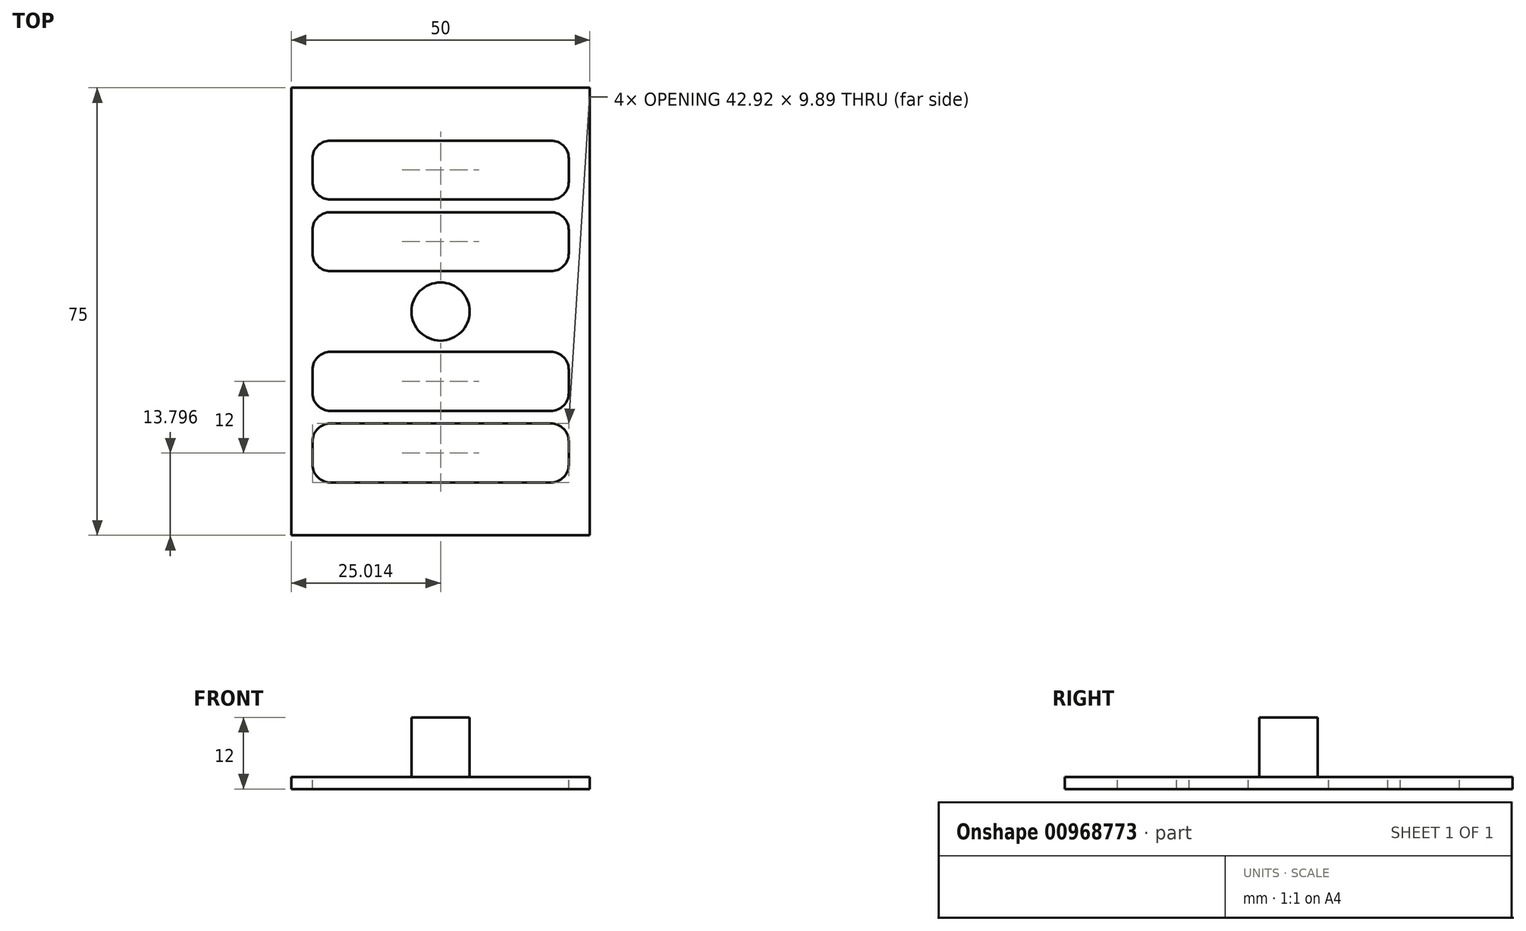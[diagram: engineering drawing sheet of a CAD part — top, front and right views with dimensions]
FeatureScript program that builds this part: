
annotation { "Feature Type Name" : "Feature", "Feature Type Description" : "" }
export const myFeature = defineFeature(function(context is Context, id is Id, definition is map)
    precondition{}
    {
        {
            var Q0;
            Q0=qCreatedBy(makeId("Top.planeOp"),FACE);
            var sketch = newSketch(context, id + "F0", { "sketchPlane" : qUnion([Q0])});
            skLineSegment(sketch, "E0.bottom", {"start": v(25, -37.5) * mm, "end": v(-25, -37.5) * mm});
            skLineSegment(sketch, "E0.top", {"start": v(25, 37.5) * mm, "end": v(-25, 37.5) * mm});
            skLineSegment(sketch, "E0.left", {"start": v(25, -37.5) * mm, "end": v(25, 37.5) * mm});
            skLineSegment(sketch, "E0.right", {"start": v(-25, -37.5) * mm, "end": v(-25, 37.5) * mm});
            skPoint(sketch, "E0.middle", {"position": v(0, 0) * mm});
            skSolve(sketch);
        }
        {
            var Q0;
            Q0=makeQuery(id+"F0.imprint","IMPRINT",FACE,{"disambiguationData":[TD([[makeQuery(id+"F0.imprint","IMPRINT",EDGE,{"derivedFrom":sQuery(id+"F0.wireOp",EDGE,"E0.bottom")}),-1.0]])]});
            extrude(context, id + "F1", {"entities" : qUnion([Q0]), "depth" : 2 * mm, "offsetDistance" : 25 * mm});
        }
        {
            var Q0;
            Q0=makeQuery(id+"FOSmCHiaZBp4P99_1.boolean.opBoolean","MERGE",FACE,{"derivedFrom":[makeQuery(id+"F1.opExtrude","CAP_FACE",FACE,{"disambiguationData":[OSD([sQuery(id+"F0.wireOp",EDGE,"E0.bottom"),sQuery(id+"F0.wireOp",EDGE,"E0.top"),sQuery(id+"F0.wireOp",EDGE,"E0.left"),sQuery(id+"F0.wireOp",EDGE,"E0.right")])],"isStart":false}),makeQuery(id+"FOSmCHiaZBp4P99_1.opExtrude","CAP_FACE",FACE,{"disambiguationData":[OSD([sQuery(id+"F7uODuXZmuw1LMT_1.wireOp",EDGE,"ikZA7m4t-yXm2-VDTh-IuRp-0IEzlSagpjaw.bottom"),sQuery(id+"F7uODuXZmuw1LMT_1.wireOp",EDGE,"ikZA7m4t-yXm2-VDTh-IuRp-0IEzlSagpjaw.left"),sQuery(id+"F7uODuXZmuw1LMT_1.wireOp",EDGE,"ikZA7m4t-yXm2-VDTh-IuRp-0IEzlSagpjaw.right"),sQuery(id+"F7uODuXZmuw1LMT_1.wireOp",EDGE,"wiYl6r0H-u17V-zEIH-iWu8-kZRWzZkrRSte"),sQuery(id+"F7uODuXZmuw1LMT_1.wireOp",EDGE,"84bd39a7-035e-4810-80ba-21c04ed16744.filletArc"),sQuery(id+"F7uODuXZmuw1LMT_1.wireOp",EDGE,"90e38472-87f6-4bb7-9f87-e36e951d7eac.filletArc")])],"isStart":false}),makeQuery(id+"FOSmCHiaZBp4P99_1.opExtrude","CAP_FACE",FACE,{"disambiguationData":[OSD([sQuery(id+"F7uODuXZmuw1LMT_1.wireOp",EDGE,"83aa809a-4b3d-4665-bd88-ce5ddef207420.MirrorCS"),sQuery(id+"F7uODuXZmuw1LMT_1.wireOp",EDGE,"7f4b2661-4254-4edf-b199-c165164cc8980.MirrorCS"),sQuery(id+"F7uODuXZmuw1LMT_1.wireOp",EDGE,"fd2b38a9-e8a0-4511-baa7-e9677021980d0.MirrorCS"),sQuery(id+"F7uODuXZmuw1LMT_1.wireOp",EDGE,"173fde81-6119-4368-834b-0b8efb7ed5110.MirrorCS"),sQuery(id+"F7uODuXZmuw1LMT_1.wireOp",EDGE,"5b3da9ca-773f-4fe3-a15f-effaa47ec4bf0.MirrorCS"),sQuery(id+"F7uODuXZmuw1LMT_1.wireOp",EDGE,"6c969054-023f-4f27-a523-787d0daa6e270.MirrorCS")])],"isStart":false})]});
            var sketch = newSketch(context, id + "F2", { "sketchPlane" : qUnion([Q0])});
            skCircle(sketch, "E1", {"center": v(0, 0) * mm, "radius": 4.88 * mm});
            skSolve(sketch);
        }
        {
            var Q0;
            Q0=makeQuery(id+"F2.imprint","IMPRINT",FACE,{"disambiguationData":[TD([[makeQuery(id+"F2.imprint","IMPRINT",EDGE,{"derivedFrom":sQuery(id+"F2.wireOp",EDGE,"E1")}),1.0]])]});
            extrude(context, id + "F3", {"entities" : qUnion([Q0]), "operationType" : NewBodyOperationType.ADD, "depth" : 10 * mm, "offsetDistance" : 25 * mm});
        }
        {
            var Q0;
            Q0=makeQuery(id+"FOSmCHiaZBp4P99_1.boolean.opBoolean","MERGE",FACE,{"derivedFrom":[makeQuery(id+"F1.opExtrude","CAP_FACE",FACE,{"disambiguationData":[OSD([sQuery(id+"F0.wireOp",EDGE,"E0.bottom"),sQuery(id+"F0.wireOp",EDGE,"E0.top"),sQuery(id+"F0.wireOp",EDGE,"E0.left"),sQuery(id+"F0.wireOp",EDGE,"E0.right")])],"isStart":false}),makeQuery(id+"FOSmCHiaZBp4P99_1.opExtrude","CAP_FACE",FACE,{"disambiguationData":[OSD([sQuery(id+"F7uODuXZmuw1LMT_1.wireOp",EDGE,"ikZA7m4t-yXm2-VDTh-IuRp-0IEzlSagpjaw.bottom"),sQuery(id+"F7uODuXZmuw1LMT_1.wireOp",EDGE,"ikZA7m4t-yXm2-VDTh-IuRp-0IEzlSagpjaw.left"),sQuery(id+"F7uODuXZmuw1LMT_1.wireOp",EDGE,"ikZA7m4t-yXm2-VDTh-IuRp-0IEzlSagpjaw.right"),sQuery(id+"F7uODuXZmuw1LMT_1.wireOp",EDGE,"wiYl6r0H-u17V-zEIH-iWu8-kZRWzZkrRSte"),sQuery(id+"F7uODuXZmuw1LMT_1.wireOp",EDGE,"84bd39a7-035e-4810-80ba-21c04ed16744.filletArc"),sQuery(id+"F7uODuXZmuw1LMT_1.wireOp",EDGE,"90e38472-87f6-4bb7-9f87-e36e951d7eac.filletArc")])],"isStart":false}),makeQuery(id+"FOSmCHiaZBp4P99_1.opExtrude","CAP_FACE",FACE,{"disambiguationData":[OSD([sQuery(id+"F7uODuXZmuw1LMT_1.wireOp",EDGE,"83aa809a-4b3d-4665-bd88-ce5ddef207420.MirrorCS"),sQuery(id+"F7uODuXZmuw1LMT_1.wireOp",EDGE,"7f4b2661-4254-4edf-b199-c165164cc8980.MirrorCS"),sQuery(id+"F7uODuXZmuw1LMT_1.wireOp",EDGE,"fd2b38a9-e8a0-4511-baa7-e9677021980d0.MirrorCS"),sQuery(id+"F7uODuXZmuw1LMT_1.wireOp",EDGE,"173fde81-6119-4368-834b-0b8efb7ed5110.MirrorCS"),sQuery(id+"F7uODuXZmuw1LMT_1.wireOp",EDGE,"5b3da9ca-773f-4fe3-a15f-effaa47ec4bf0.MirrorCS"),sQuery(id+"F7uODuXZmuw1LMT_1.wireOp",EDGE,"6c969054-023f-4f27-a523-787d0daa6e270.MirrorCS")])],"isStart":false})]});
            var sketch = newSketch(context, id + "F4", { "sketchPlane" : qUnion([Q0])});
            skLineSegment(sketch, "E2.bottom", {"start": v(-18.44, 16.65) * mm, "end": v(18.47, 16.65) * mm});
            skLineSegment(sketch, "E2.top", {"start": v(-18.44, 6.76) * mm, "end": v(18.47, 6.76) * mm});
            skLineSegment(sketch, "E2.left", {"start": v(-21.44, 13.65) * mm, "end": v(-21.44, 9.76) * mm});
            skLineSegment(sketch, "E2.right", {"start": v(21.47, 13.65) * mm, "end": v(21.47, 9.76) * mm});
            skLineSegment(sketch, "E3.MirrorCS", {"start": v(21.47, -13.65) * mm, "end": v(21.47, -9.76) * mm});
            skLineSegment(sketch, "E4.MirrorCS", {"start": v(-21.44, -13.65) * mm, "end": v(-21.44, -9.76) * mm});
            skLineSegment(sketch, "E5.MirrorCS", {"start": v(-18.44, -16.65) * mm, "end": v(18.47, -16.65) * mm});
            skLineSegment(sketch, "E6.MirrorCS", {"start": v(-18.44, -6.76) * mm, "end": v(18.47, -6.76) * mm});
            skPoint(sketch, "E7.visualSharp", {"position": v(-21.44, 16.65) * mm});
            skArc(sketch, "E7.filletArc", {"start": v(-18.44, 16.65) * mm, "mid": v(-20.57, 15.77) * mm, "end": v(-21.44, 13.65) * mm});
            skPoint(sketch, "E8.visualSharp", {"position": v(-21.44, 6.76) * mm});
            skArc(sketch, "E8.filletArc", {"start": v(-21.44, 9.76) * mm, "mid": v(-20.57, 7.64) * mm, "end": v(-18.44, 6.76) * mm});
            skPoint(sketch, "E9.visualSharp", {"position": v(21.47, 6.76) * mm});
            skArc(sketch, "E9.filletArc", {"start": v(18.47, 6.76) * mm, "mid": v(20.6, 7.64) * mm, "end": v(21.47, 9.76) * mm});
            skPoint(sketch, "E10.visualSharp", {"position": v(21.47, 16.65) * mm});
            skArc(sketch, "E10.filletArc", {"start": v(21.47, 13.65) * mm, "mid": v(20.6, 15.77) * mm, "end": v(18.47, 16.65) * mm});
            skPoint(sketch, "E11.visualSharp", {"position": v(-21.44, -6.76) * mm});
            skArc(sketch, "E11.filletArc", {"start": v(-18.44, -6.76) * mm, "mid": v(-20.57, -7.64) * mm, "end": v(-21.44, -9.76) * mm});
            skPoint(sketch, "E12.visualSharp", {"position": v(-21.44, -16.65) * mm});
            skArc(sketch, "E12.filletArc", {"start": v(-21.44, -13.65) * mm, "mid": v(-20.57, -15.77) * mm, "end": v(-18.44, -16.65) * mm});
            skPoint(sketch, "E13.visualSharp", {"position": v(21.47, -16.65) * mm});
            skArc(sketch, "E13.filletArc", {"start": v(18.47, -16.65) * mm, "mid": v(20.6, -15.77) * mm, "end": v(21.47, -13.65) * mm});
            skPoint(sketch, "E14.visualSharp", {"position": v(21.47, -6.76) * mm});
            skArc(sketch, "E14.filletArc", {"start": v(21.47, -9.76) * mm, "mid": v(20.6, -7.64) * mm, "end": v(18.47, -6.76) * mm});
            skArc(sketch, "E15.0.1.0", {"start": v(-18.44, -18.76) * mm, "mid": v(-20.57, -19.64) * mm, "end": v(-21.44, -21.76) * mm});
            skPoint(sketch, "E15.0.1.1", {"position": v(-21.44, -28.65) * mm});
            skArc(sketch, "E15.0.1.2", {"start": v(-21.44, -25.65) * mm, "mid": v(-20.57, -27.77) * mm, "end": v(-18.44, -28.65) * mm});
            skArc(sketch, "E15.0.1.3", {"start": v(18.47, -28.65) * mm, "mid": v(20.6, -27.77) * mm, "end": v(21.47, -25.65) * mm});
            skLineSegment(sketch, "E15.0.1.4", {"start": v(21.47, -25.65) * mm, "end": v(21.47, -21.76) * mm});
            skLineSegment(sketch, "E15.0.1.5", {"start": v(-21.44, -25.65) * mm, "end": v(-21.44, -21.76) * mm});
            skPoint(sketch, "E15.0.1.6", {"position": v(-21.44, -18.76) * mm});
            skPoint(sketch, "E15.0.1.7", {"position": v(21.47, -28.65) * mm});
            skPoint(sketch, "E15.0.1.8", {"position": v(21.47, -18.76) * mm});
            skArc(sketch, "E15.0.1.9", {"start": v(21.47, -21.76) * mm, "mid": v(20.6, -19.64) * mm, "end": v(18.47, -18.76) * mm});
            skLineSegment(sketch, "E15.0.1.10", {"start": v(-18.44, -28.65) * mm, "end": v(18.47, -28.65) * mm});
            skLineSegment(sketch, "E15.0.1.11", {"start": v(-18.44, -18.76) * mm, "end": v(18.47, -18.76) * mm});
            skLineSegment(sketch, "E15.direction1", {"start": v(-21.44, -16.65) * mm, "end": v(3.56, -16.65) * mm, "construction": true});
            skLineSegment(sketch, "E15.direction2", {"start": v(-21.44, -16.65) * mm, "end": v(-21.44, -28.65) * mm, "construction": true});
            skPoint(sketch, "E16.0.1.0", {"position": v(-21.44, 18.76) * mm});
            skArc(sketch, "E16.0.1.1", {"start": v(21.47, 25.65) * mm, "mid": v(20.6, 27.77) * mm, "end": v(18.47, 28.65) * mm});
            skLineSegment(sketch, "E16.0.1.2", {"start": v(21.47, 25.65) * mm, "end": v(21.47, 21.76) * mm});
            skArc(sketch, "E16.0.1.3", {"start": v(-18.44, 28.65) * mm, "mid": v(-20.57, 27.77) * mm, "end": v(-21.44, 25.65) * mm});
            skPoint(sketch, "E16.0.1.4", {"position": v(-21.44, 28.65) * mm});
            skPoint(sketch, "E16.0.1.5", {"position": v(21.47, 18.76) * mm});
            skArc(sketch, "E16.0.1.6", {"start": v(-21.44, 21.76) * mm, "mid": v(-20.57, 19.64) * mm, "end": v(-18.44, 18.76) * mm});
            skArc(sketch, "E16.0.1.7", {"start": v(18.47, 18.76) * mm, "mid": v(20.6, 19.64) * mm, "end": v(21.47, 21.76) * mm});
            skLineSegment(sketch, "E16.0.1.8", {"start": v(-21.44, 25.65) * mm, "end": v(-21.44, 21.76) * mm});
            skPoint(sketch, "E16.0.1.9", {"position": v(21.47, 28.65) * mm});
            skLineSegment(sketch, "E16.0.1.10", {"start": v(-18.44, 18.76) * mm, "end": v(18.47, 18.76) * mm});
            skLineSegment(sketch, "E16.0.1.11", {"start": v(-18.44, 28.65) * mm, "end": v(18.47, 28.65) * mm});
            skLineSegment(sketch, "E16.direction1", {"start": v(-21.44, 6.76) * mm, "end": v(3.56, 6.76) * mm, "construction": true});
            skLineSegment(sketch, "E16.direction2", {"start": v(-21.44, 6.76) * mm, "end": v(-21.44, 18.76) * mm, "construction": true});
            skSolve(sketch);
        }
        {
            var Q0;
            Q0=makeQuery(id+"F4.imprint","IMPRINT",FACE,{"disambiguationData":[TD([[makeQuery(id+"F4.imprint","IMPRINT",EDGE,{"derivedFrom":sQuery(id+"F4.wireOp",EDGE,"E3.MirrorCS")}),1.0]])]});
            var Q1;
            Q1=makeQuery(id+"F4.imprint","IMPRINT",FACE,{"disambiguationData":[TD([[makeQuery(id+"F4.imprint","IMPRINT",EDGE,{"derivedFrom":sQuery(id+"F4.wireOp",EDGE,"E2.bottom")}),-1.0]])]});
            var Q2;
            Q2=makeQuery(id+"F4.imprint","IMPRINT",FACE,{"disambiguationData":[TD([[makeQuery(id+"F4.imprint","IMPRINT",EDGE,{"derivedFrom":sQuery(id+"F4.wireOp",EDGE,"E15.0.1.0")}),1.0]])]});
            var Q3;
            Q3=makeQuery(id+"F4.imprint","IMPRINT",FACE,{"disambiguationData":[TD([[makeQuery(id+"F4.imprint","IMPRINT",EDGE,{"derivedFrom":sQuery(id+"F4.wireOp",EDGE,"E16.0.1.1")}),1.0]])]});
            extrude(context, id + "F5", {"entities" : qUnion([Q0, Q1, Q2, Q3]), "operationType" : NewBodyOperationType.REMOVE, "oppositeDirection" : true, "depth" : 25 * mm, "offsetDistance" : 25 * mm});
        }
    });
